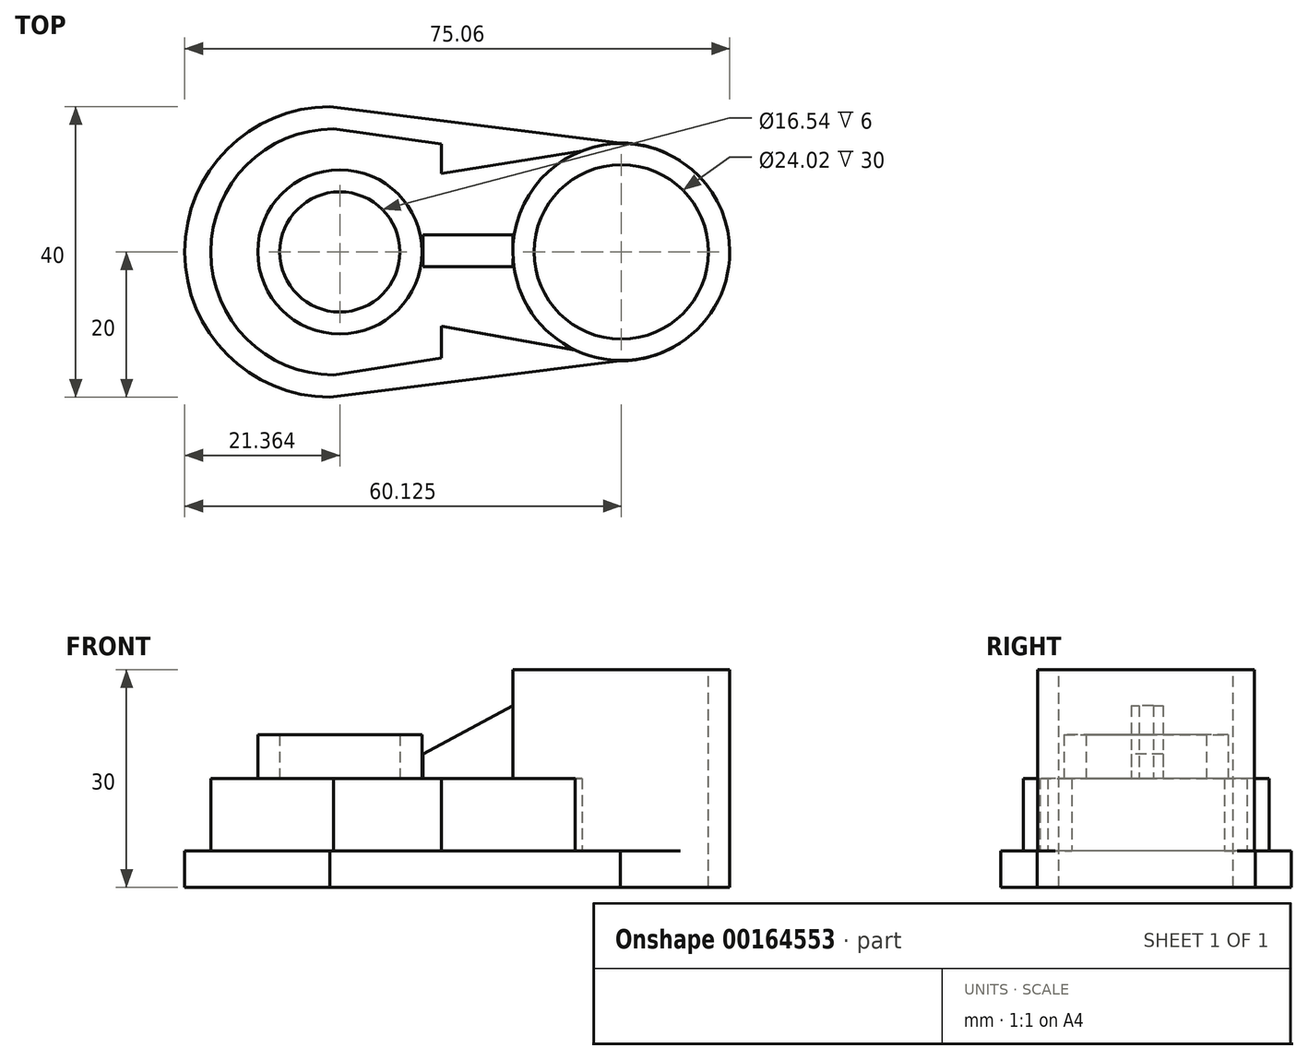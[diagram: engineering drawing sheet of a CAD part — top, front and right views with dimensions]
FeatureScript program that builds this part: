
annotation { "Feature Type Name" : "Feature", "Feature Type Description" : "" }
export const myFeature = defineFeature(function(context is Context, id is Id, definition is map)
    precondition{}
    {
        {
            var Q0;
            Q0=qCreatedBy(makeId("Top.planeOp"),FACE);
            var sketch = newSketch(context, id + "F0", { "sketchPlane" : qUnion([Q0])});
            skArc(sketch, "E0", {"start": v(-31.4, 20) * mm, "mid": v(-51.4, 0) * mm, "end": v(-31.4, -20) * mm});
            skArc(sketch, "E1", {"start": v(8.6, -15) * mm, "mid": v(23.6, 0) * mm, "end": v(8.6, 15) * mm});
            skLineSegment(sketch, "E2", {"start": v(-31.4, 20) * mm, "end": v(8.6, 15) * mm});
            skLineSegment(sketch, "E3", {"start": v(-31.4, -20) * mm, "end": v(8.6, -15) * mm});
            skSolve(sketch);
        }
        {
            var Q0;
            Q0=makeQuery(id+"F0.imprint","IMPRINT",FACE,{"disambiguationData":[TD([[makeQuery(id+"F0.imprint","IMPRINT",EDGE,{"derivedFrom":sQuery(id+"F0.wireOp",EDGE,"E0")}),1.0]])]});
            var sketch = newSketch(context, id + "F1", { "sketchPlane" : qUnion([Q0])});
            skCircle(sketch, "E4", {"center": v(8.73, 0) * mm, "radius": 14.93 * mm});
            skSolve(sketch);
        }
        {
            var Q0;
            Q0=makeQuery(id+"F0.imprint","IMPRINT",FACE,{"disambiguationData":[TD([[makeQuery(id+"F0.imprint","IMPRINT",EDGE,{"derivedFrom":sQuery(id+"F0.wireOp",EDGE,"E0")}),1.0]])]});
            var sketch = newSketch(context, id + "F2", { "sketchPlane" : qUnion([Q0])});
            skArc(sketch, "E5", {"start": v(-30.88, 16.94) * mm, "mid": v(-47.82, 0) * mm, "end": v(-30.88, -16.94) * mm});
            skLineSegment(sketch, "E6", {"start": v(-30.88, 16.94) * mm, "end": v(-16.02, 14.84) * mm});
            skLineSegment(sketch, "E7", {"start": v(-30.88, -16.94) * mm, "end": v(-16.06, -14.6) * mm});
            skLineSegment(sketch, "E8", {"start": v(-16.06, -14.6) * mm, "end": v(-16.06, -10.24) * mm});
            skLineSegment(sketch, "E9", {"start": v(-16.06, -10.24) * mm, "end": v(8.46, -14.6) * mm});
            skLineSegment(sketch, "E10", {"start": v(-16.02, 14.84) * mm, "end": v(-16.02, 10.78) * mm});
            skLineSegment(sketch, "E11", {"start": v(-16.02, 10.78) * mm, "end": v(9, 14.84) * mm});
            skLineSegment(sketch, "E12", {"start": v(9, 14.84) * mm, "end": v(8.46, -14.6) * mm});
            skSolve(sketch);
        }
        {
            var Q0;
            Q0=makeQuery(id+"F0.imprint","IMPRINT",FACE,{"disambiguationData":[TD([[makeQuery(id+"F0.imprint","IMPRINT",EDGE,{"derivedFrom":sQuery(id+"F0.wireOp",EDGE,"E0")}),1.0]])]});
            var sketch = newSketch(context, id + "F3", { "sketchPlane" : qUnion([Q0])});
            skCircle(sketch, "E13", {"center": v(-30.03, 0) * mm, "radius": 11.3 * mm});
            skCircle(sketch, "E14", {"center": v(-30.03, 0) * mm, "radius": 8.27 * mm});
            skSolve(sketch);
        }
        {
            var Q0;
            Q0=makeQuery(id+"F0.imprint","IMPRINT",FACE,{"disambiguationData":[TD([[makeQuery(id+"F0.imprint","IMPRINT",EDGE,{"derivedFrom":sQuery(id+"F0.wireOp",EDGE,"E0")}),1.0]])]});
            var sketch = newSketch(context, id + "F4", { "sketchPlane" : qUnion([Q0])});
            skLineSegment(sketch, "E15.bottom", {"start": v(-6.17, -2.05) * mm, "end": v(-18.56, -2.05) * mm});
            skLineSegment(sketch, "E15.top", {"start": v(-6.17, 2.33) * mm, "end": v(-18.56, 2.33) * mm});
            skLineSegment(sketch, "E15.left", {"start": v(-6.17, -2.05) * mm, "end": v(-6.17, 2.33) * mm});
            skLineSegment(sketch, "E15.right", {"start": v(-18.56, -2.05) * mm, "end": v(-18.56, 2.33) * mm});
            skSolve(sketch);
        }
        {
            var Q0;
            Q0=makeQuery(id+"F0.imprint","IMPRINT",FACE,{"disambiguationData":[TD([[makeQuery(id+"F0.imprint","IMPRINT",EDGE,{"derivedFrom":sQuery(id+"F0.wireOp",EDGE,"E0")}),1.0]])]});
            extrude(context, id + "F5", {"entities" : qUnion([Q0]), "depth" : 5 * mm});
        }
        {
            var Q0;
            Q0 = qSketchRegion(id + "F1", true);
            extrude(context, id + "F6", {"entities" : qUnion([Q0]), "operationType" : NewBodyOperationType.ADD, "depth" : 30 * mm});
        }
        {
            var Q0;
            Q0 = qSketchRegion(id + "F2", true);
            extrude(context, id + "F7", {"entities" : qUnion([Q0]), "operationType" : NewBodyOperationType.ADD, "depth" : 15 * mm});
        }
        {
            var Q0;
            Q0 = qSketchRegion(id + "F3", true);
            extrude(context, id + "F8", {"entities" : qUnion([Q0]), "operationType" : NewBodyOperationType.ADD, "depth" : 21 * mm});
        }
        {
            var Q0;
            Q0 = qSketchRegion(id + "F4", true);
            extrude(context, id + "F9", {"entities" : qUnion([Q0]), "operationType" : NewBodyOperationType.ADD, "depth" : 25 * mm});
        }
        {
            var Q0;
            Q0=makeQuery(id+"F9.opExtrude","SWEPT_FACE",FACE,{"disambiguationData":[OSD([sQuery(id+"F4.wireOp",EDGE,"E15.bottom")])]});
            var sketch = newSketch(context, id + "F10", { "sketchPlane" : qUnion([Q0])});
            skLineSegment(sketch, "E16", {"start": v(-6.17, 25) * mm, "end": v(-18.56, 18.37) * mm});
            skSolve(sketch);
        }
        {
            var Q0;
            Q0 = qSketchRegion(id + "F10", true);
            var Q1;
            {var subQ0=sQuery(id+"F10.wireOp",EDGE,"E16");Q1=makeQuery(id+"F10.imprint","IMPRINT",FACE,{"disambiguationData":[TD([[makeQuery(id+"F10.imprint","IMPRINT",EDGE,{"derivedFrom":subQ0}),-1.0]])]});}
            extrude(context, id + "F11", {"entities" : qUnion([Q0, Q1]), "operationType" : NewBodyOperationType.REMOVE, "oppositeDirection" : true, "depth" : 25 * mm});
        }
        {
            var Q0;
            Q0=makeQuery(id+"F6.opExtrude","CAP_FACE",FACE,{"disambiguationData":[OSD([sQuery(id+"F1.wireOp",EDGE,"E4")])],"isStart":false});
            var sketch = newSketch(context, id + "F12", { "sketchPlane" : qUnion([Q0])});
            skCircle(sketch, "E17", {"center": v(8.73, 0) * mm, "radius": 12.01 * mm});
            skSolve(sketch);
        }
        {
            var Q0;
            Q0=makeQuery(id+"F12.imprint","IMPRINT",FACE,{"disambiguationData":[TD([[makeQuery(id+"F12.imprint","IMPRINT",EDGE,{"derivedFrom":sQuery(id+"F12.wireOp",EDGE,"E17")}),1.0]])]});
            extrude(context, id + "F13", {"entities" : qUnion([Q0]), "operationType" : NewBodyOperationType.REMOVE, "oppositeDirection" : true, "depth" : 30 * mm});
        }
    });
